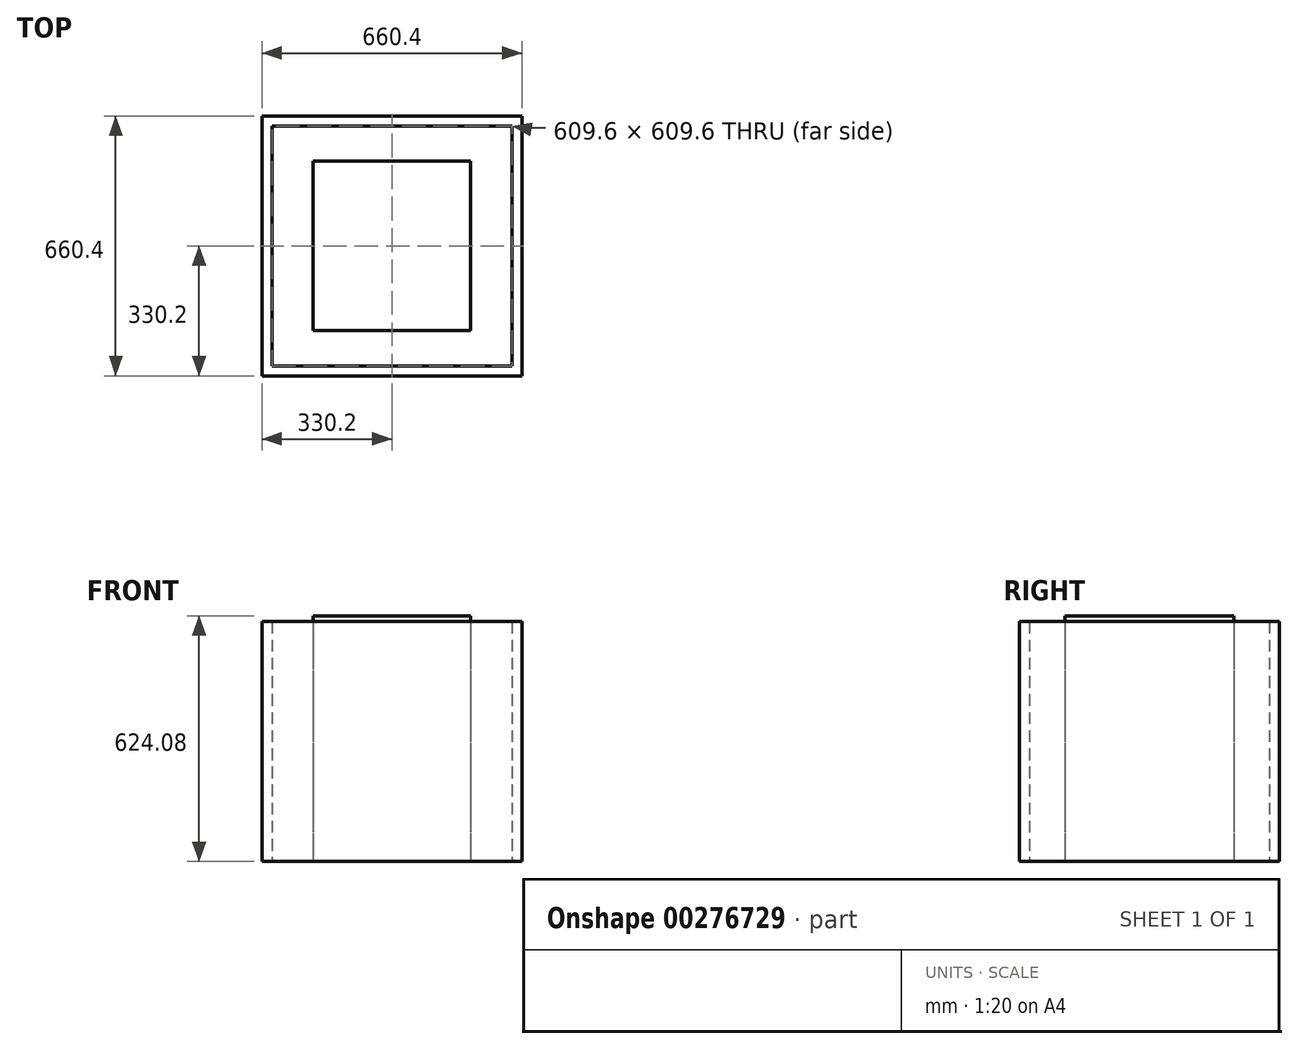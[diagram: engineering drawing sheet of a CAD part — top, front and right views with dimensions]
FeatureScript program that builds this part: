
annotation { "Feature Type Name" : "Feature", "Feature Type Description" : "" }
export const myFeature = defineFeature(function(context is Context, id is Id, definition is map)
    precondition{}
    {
        {
            var Q0;
            Q0=qCreatedBy(makeId("Top.planeOp"),FACE);
            var sketch = newSketch(context, id + "F0", { "sketchPlane" : qUnion([Q0])});
            skLineSegment(sketch, "E0.bottom", {"start": v(200.03, 215.01) * mm, "end": v(-200.03, 215.01) * mm});
            skLineSegment(sketch, "E0.top", {"start": v(200.03, -215.01) * mm, "end": v(-200.03, -215.01) * mm});
            skLineSegment(sketch, "E0.left", {"start": v(200.03, 215.01) * mm, "end": v(200.03, -215.01) * mm});
            skLineSegment(sketch, "E0.right", {"start": v(-200.03, 215.01) * mm, "end": v(-200.03, -215.01) * mm});
            skPoint(sketch, "E0.middle", {"position": v(0, 0) * mm});
            skSolve(sketch);
        }
        {
            var Q0;
            Q0=makeQuery(id+"F0.imprint","IMPRINT",FACE,{"disambiguationData":[TD([[makeQuery(id+"F0.imprint","IMPRINT",EDGE,{"derivedFrom":sQuery(id+"F0.wireOp",EDGE,"E0.bottom")}),1.0]])]});
            extrude(context, id + "F2", {"entities" : qUnion([Q0]), "depth" : 624.08 * mm});
        }
        {
            var Q0;
            Q0=qCreatedBy(makeId("Top.planeOp"),FACE);
            var sketch = newSketch(context, id + "F1", { "sketchPlane" : qUnion([Q0])});
            skLineSegment(sketch, "E1.bottom", {"start": v(-304.8, -304.8) * mm, "end": v(304.8, -304.8) * mm});
            skLineSegment(sketch, "E1.top", {"start": v(-304.8, 304.8) * mm, "end": v(304.8, 304.8) * mm});
            skLineSegment(sketch, "E1.left", {"start": v(-304.8, -304.8) * mm, "end": v(-304.8, 304.8) * mm});
            skLineSegment(sketch, "E1.right", {"start": v(304.8, -304.8) * mm, "end": v(304.8, 304.8) * mm});
            skPoint(sketch, "E1.middle", {"position": v(0, 0) * mm});
            skLineSegment(sketch, "E2.0", {"start": v(330.2, -330.2) * mm, "end": v(330.2, 330.2) * mm});
            skLineSegment(sketch, "E2.1", {"start": v(-330.2, -330.2) * mm, "end": v(330.2, -330.2) * mm});
            skLineSegment(sketch, "E2.2", {"start": v(-330.2, -330.2) * mm, "end": v(-330.2, 330.2) * mm});
            skLineSegment(sketch, "E2.3", {"start": v(-330.2, 330.2) * mm, "end": v(330.2, 330.2) * mm});
            skSolve(sketch);
        }
        {
            var Q0;
            Q0=makeQuery(id+"F1.imprint","IMPRINT",FACE,{"disambiguationData":[TD([[makeQuery(id+"F1.imprint","IMPRINT",EDGE,{"derivedFrom":sQuery(id+"F1.wireOp",EDGE,"E1.bottom")}),-1.0]])]});
            extrude(context, id + "F3", {"entities" : qUnion([Q0]), "depth" : 609.6 * mm});
        }
    });
